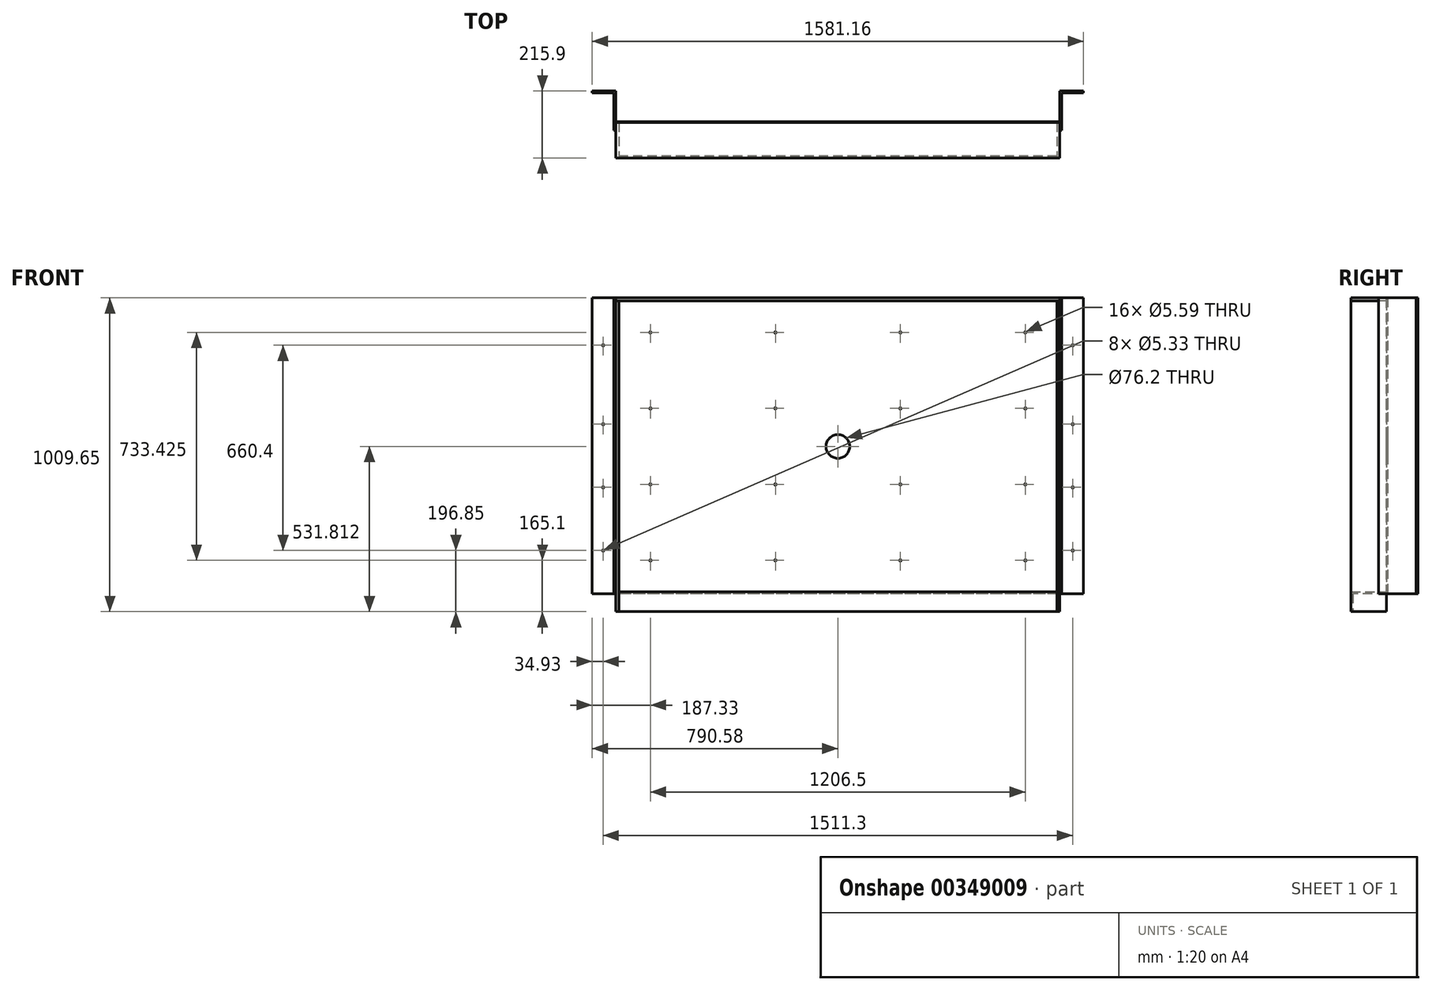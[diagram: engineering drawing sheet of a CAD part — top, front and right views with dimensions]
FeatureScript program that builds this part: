
annotation { "Feature Type Name" : "Feature", "Feature Type Description" : "" }
export const myFeature = defineFeature(function(context is Context, id is Id, definition is map)
    precondition{}
    {
        {
            assignVariable(context, id + "F0", {"name" : "OuterFrameWidth", "anyValue" : 1428.75 * mm});
        }
        {
            var Q0;
            Q0=qCreatedBy(makeId("Right.planeOp"),FACE);
            var sketch = newSketch(context, id + "F1", { "sketchPlane" : qUnion([Q0])});
            skLineSegment(sketch, "E0", {"start": v(0, 0) * mm, "end": v(-111.12, 0) * mm});
            skLineSegment(sketch, "E1", {"start": v(-111.12, 0) * mm, "end": v(-111.12, -57.15) * mm});
            skLineSegment(sketch, "E2", {"start": v(-111.12, -57.15) * mm, "end": v(-117.47, -57.15) * mm});
            skLineSegment(sketch, "E3", {"start": v(-117.47, -57.15) * mm, "end": v(-117.47, 6.35) * mm});
            skLineSegment(sketch, "E4", {"start": v(-117.48, 6.35) * mm, "end": v(-3.17, 6.35) * mm});
            skLineSegment(sketch, "E5", {"start": v(-3.18, 0) * mm, "end": v(-3.18, 952.5) * mm});
            skLineSegment(sketch, "E6", {"start": v(-3.18, 942.98) * mm, "end": v(-117.48, 942.98) * mm});
            skLineSegment(sketch, "E7", {"start": v(-117.48, 942.98) * mm, "end": v(-117.48, 952.5) * mm});
            skLineSegment(sketch, "E8", {"start": v(-117.48, 952.5) * mm, "end": v(0, 952.5) * mm});
            skLineSegment(sketch, "E9", {"start": v(0, 952.5) * mm, "end": v(0, 0) * mm});
            skLineSegment(sketch, "E10", {"start": v(98.42, 917.94) * mm, "end": v(98.42, 187.98) * mm, "construction": true});
            skSolve(sketch);
        }
        {
            var Q0;
            {var subQ7=sQuery(id+"F1.wireOp",EDGE,"E9");Q0=makeQuery(id+"F1.imprint","IMPRINT",FACE,{"disambiguationData":[TD([[makeQuery(id+"F1.imprint","IMPRINT",EDGE,{"derivedFrom":subQ7}),-1.0]])]});}
            extrude(context, id + "F2", {"entities" : qUnion([Q0]), "endBound" : BoundingType.SYMMETRIC, "depth" : getVariable(context, 'OuterFrameWidth')});
        }
        {
            var Q0;
            {var subQ3=sQuery(id+"F1.wireOp",EDGE,"E6");Q0=makeQuery(id+"F1.imprint","IMPRINT",FACE,{"disambiguationData":[TD([[makeQuery(id+"F1.imprint","IMPRINT",EDGE,{"derivedFrom":subQ3}),-1.0]])]});}
            extrude(context, id + "F3", {"entities" : qUnion([Q0]), "endBound" : BoundingType.SYMMETRIC, "depth" : getVariable(context, 'OuterFrameWidth')});
        }
        {
            var Q0;
            {var subQ0=sQuery(id+"F1.wireOp",EDGE,"E1");Q0=makeQuery(id+"F1.imprint","IMPRINT",FACE,{"disambiguationData":[TD([[makeQuery(id+"F1.imprint","IMPRINT",EDGE,{"derivedFrom":subQ0}),-1.0]])]});}
            extrude(context, id + "F4", {"entities" : qUnion([Q0]), "endBound" : BoundingType.SYMMETRIC, "depth" : getVariable(context, 'OuterFrameWidth') - 19.05 * mm});
        }
        {
            var Q0;
            Q0=makeQuery(id+"F3.opExtrude","CAP_FACE",FACE,{"disambiguationData":[OSD([sQuery(id+"F1.wireOp",EDGE,"E5"),sQuery(id+"F1.wireOp",EDGE,"E6"),sQuery(id+"F1.wireOp",EDGE,"E7"),sQuery(id+"F1.wireOp",EDGE,"E8")])],"isStart":true});
            var sketch = newSketch(context, id + "F5", { "sketchPlane" : qUnion([Q0])});
            skLineSegment(sketch, "E11.bottom", {"start": v(3.17, 942.98) * mm, "end": v(117.47, 942.98) * mm});
            skLineSegment(sketch, "E11.top", {"start": v(3.18, -57.15) * mm, "end": v(117.47, -57.15) * mm});
            skLineSegment(sketch, "E11.left", {"start": v(3.18, 942.98) * mm, "end": v(3.18, -57.15) * mm});
            skLineSegment(sketch, "E11.right", {"start": v(117.47, 942.98) * mm, "end": v(117.47, -57.15) * mm});
            skSolve(sketch);
        }
        {
            var Q0;
            Q0 = qSketchRegion(id + "F5", true);
            var Q1;
            Q1=makeQuery(id+"F4.opExtrude","CAP_FACE",FACE,{"disambiguationData":[OSD([sQuery(id+"F1.wireOp",EDGE,"E0"),sQuery(id+"F1.wireOp",EDGE,"E1"),sQuery(id+"F1.wireOp",EDGE,"E2"),sQuery(id+"F1.wireOp",EDGE,"E3"),sQuery(id+"F1.wireOp",EDGE,"E4"),sQuery(id+"F1.wireOp",EDGE,"E5")])],"isStart":true});
            extrude(context, id + "F6", {"entities" : qUnion([Q0]), "endBound" : BoundingType.UP_TO_SURFACE, "oppositeDirection" : true, "endBoundEntityFace" : qUnion([Q1]), "depth" : 25.4 * mm});
        }
        {
            var Q0;
            Q0=makeQuery(id+"F6.opExtrude","SWEPT_BODY",BODY,{"disambiguationData":[OSD([sQuery(id+"F5.wireOp",EDGE,"E11.bottom"),sQuery(id+"F5.wireOp",EDGE,"E11.top"),sQuery(id+"F5.wireOp",EDGE,"E11.left"),sQuery(id+"F5.wireOp",EDGE,"E11.right")])]});
            var Q1;
            Q1=qCreatedBy(makeId("Right.planeOp"),FACE);
            mirror(context, id + "F7", {"entities" : qUnion([Q0]), "mirrorPlane" : qUnion([Q1])});
        }
        {
            var Q0;
            Q0=makeQuery(id+"F2.opExtrude","SWEPT_FACE",FACE,{"disambiguationData":[OSD([sQuery(id+"F1.wireOp",EDGE,"E5")])]});
            var sketch = newSketch(context, id + "F8", { "sketchPlane" : qUnion([Q0])});
            skLineSegment(sketch, "E12.bottom", {"start": v(-603.25, 841.38) * mm, "end": v(603.25, 841.38) * mm, "construction": true});
            skLineSegment(sketch, "E12.top", {"start": v(-603.25, 107.95) * mm, "end": v(603.25, 107.95) * mm, "construction": true});
            skLineSegment(sketch, "E12.left", {"start": v(-603.25, 841.38) * mm, "end": v(-603.25, 107.95) * mm, "construction": true});
            skLineSegment(sketch, "E12.right", {"start": v(603.25, 841.38) * mm, "end": v(603.25, 107.95) * mm, "construction": true});
            skLineSegment(sketch, "E13", {"start": v(-603.25, 596.9) * mm, "end": v(603.25, 596.9) * mm, "construction": true});
            skLineSegment(sketch, "E14", {"start": v(-603.25, 352.43) * mm, "end": v(603.25, 352.43) * mm, "construction": true});
            skLineSegment(sketch, "E15", {"start": v(-201.08, 841.38) * mm, "end": v(-201.08, 107.95) * mm, "construction": true});
            skLineSegment(sketch, "E16", {"start": v(201.08, 841.38) * mm, "end": v(201.08, 107.95) * mm, "construction": true});
            skLineSegment(sketch, "E17", {"start": v(0, 0) * mm, "end": v(0, 841.38) * mm, "construction": true});
            skLineSegment(sketch, "E18", {"start": v(-771.98, 474.66) * mm, "end": v(821.12, 474.66) * mm, "construction": true});
            skCircle(sketch, "E19", {"center": v(-603.25, 841.38) * mm, "radius": 2.8 * mm});
            skCircle(sketch, "E20", {"center": v(-201.08, 841.38) * mm, "radius": 2.8 * mm});
            skCircle(sketch, "E21", {"center": v(201.08, 841.38) * mm, "radius": 2.8 * mm});
            skCircle(sketch, "E22", {"center": v(603.25, 841.38) * mm, "radius": 2.8 * mm});
            skCircle(sketch, "E23", {"center": v(603.25, 596.9) * mm, "radius": 2.8 * mm});
            skCircle(sketch, "E24", {"center": v(603.25, 352.43) * mm, "radius": 2.8 * mm});
            skCircle(sketch, "E25", {"center": v(603.25, 107.95) * mm, "radius": 2.8 * mm});
            skCircle(sketch, "E26", {"center": v(201.08, 107.95) * mm, "radius": 2.8 * mm});
            skCircle(sketch, "E27", {"center": v(201.08, 596.9) * mm, "radius": 2.8 * mm});
            skCircle(sketch, "E28", {"center": v(201.08, 352.43) * mm, "radius": 2.8 * mm});
            skCircle(sketch, "E29", {"center": v(-201.08, 352.43) * mm, "radius": 2.8 * mm});
            skCircle(sketch, "E30", {"center": v(-201.08, 596.9) * mm, "radius": 2.8 * mm});
            skCircle(sketch, "E31", {"center": v(-201.08, 107.95) * mm, "radius": 2.8 * mm});
            skCircle(sketch, "E32", {"center": v(-603.25, 107.95) * mm, "radius": 2.8 * mm});
            skCircle(sketch, "E33", {"center": v(-603.25, 596.9) * mm, "radius": 2.8 * mm});
            skCircle(sketch, "E34", {"center": v(-603.25, 352.43) * mm, "radius": 2.8 * mm});
            skCircle(sketch, "E35", {"center": v(0, 474.66) * mm, "radius": 38.1 * mm});
            skLineSegment(sketch, "E36.bottom", {"start": v(-679.45, 917.58) * mm, "end": v(679.45, 917.58) * mm, "construction": true});
            skLineSegment(sketch, "E36.top", {"start": v(-679.45, 31.75) * mm, "end": v(679.45, 31.75) * mm, "construction": true});
            skLineSegment(sketch, "E36.left", {"start": v(-679.45, 917.58) * mm, "end": v(-679.45, 31.75) * mm, "construction": true});
            skLineSegment(sketch, "E36.right", {"start": v(679.45, 917.58) * mm, "end": v(679.45, 31.75) * mm, "construction": true});
            skLineSegment(sketch, "E37.bottom", {"start": v(-704.85, 942.98) * mm, "end": v(704.85, 942.98) * mm, "construction": true});
            skLineSegment(sketch, "E37.top", {"start": v(-704.85, 6.35) * mm, "end": v(704.85, 6.35) * mm, "construction": true});
            skLineSegment(sketch, "E37.left", {"start": v(-704.85, 942.98) * mm, "end": v(-704.85, 6.35) * mm, "construction": true});
            skLineSegment(sketch, "E37.right", {"start": v(704.85, 942.98) * mm, "end": v(704.85, 6.35) * mm, "construction": true});
            skLineSegment(sketch, "E38.top", {"start": v(-679.45, 133.35) * mm, "end": v(679.45, 133.35) * mm, "construction": true});
            skLineSegment(sketch, "E38.left", {"start": v(-679.45, 31.75) * mm, "end": v(-679.45, 133.35) * mm, "construction": true});
            skLineSegment(sketch, "E38.right", {"start": v(679.45, 31.75) * mm, "end": v(679.45, 133.35) * mm, "construction": true});
            skSolve(sketch);
        }
        {
            var Q0;
            Q0 = qSketchRegion(id + "F8", true);
            extrude(context, id + "F9", {"entities" : qUnion([Q0]), "operationType" : NewBodyOperationType.REMOVE, "endBound" : BoundingType.THROUGH_ALL, "oppositeDirection" : true, "depth" : 25.4 * mm});
        }
        {
            var Q0;
            Q0=qCreatedBy(makeId("Top.planeOp"),FACE);
            var sketch = newSketch(context, id + "F10", { "sketchPlane" : qUnion([Q0])});
            skLineSegment(sketch, "E39", {"start": v(-790.58, 98.42) * mm, "end": v(-714.38, 98.42) * mm});
            skLineSegment(sketch, "E40", {"start": v(-714.38, 98.42) * mm, "end": v(-714.38, -28.58) * mm});
            skLineSegment(sketch, "E41", {"start": v(-714.38, -28.58) * mm, "end": v(-720.73, -28.58) * mm});
            skLineSegment(sketch, "E42", {"start": v(-720.73, -28.58) * mm, "end": v(-720.73, 92.07) * mm});
            skLineSegment(sketch, "E43", {"start": v(-720.73, 92.07) * mm, "end": v(-790.58, 92.07) * mm});
            skLineSegment(sketch, "E44", {"start": v(-790.58, 98.42) * mm, "end": v(-790.58, 92.07) * mm});
            skSolve(sketch);
        }
        {
            var Q0;
            Q0 = qSketchRegion(id + "F10", true);
            var Q1;
            Q1=makeQuery(id+"F3.opExtrude","SWEPT_FACE",FACE,{"disambiguationData":[OSD([sQuery(id+"F1.wireOp",EDGE,"E8")])]});
            extrude(context, id + "F11", {"entities" : qUnion([Q0]), "endBound" : BoundingType.UP_TO_SURFACE, "endBoundEntityFace" : qUnion([Q1]), "depth" : 25.4 * mm});
        }
        {
            var Q0;
            Q0=makeQuery(id+"F11.opExtrude","SWEPT_FACE",FACE,{"disambiguationData":[OSD([sQuery(id+"F10.wireOp",EDGE,"E43")])]});
            var sketch = newSketch(context, id + "F12", { "sketchPlane" : qUnion([Q0])});
            skCircle(sketch, "E45", {"center": v(-755.65, 800.1) * mm, "radius": 2.67 * mm});
            skCircle(sketch, "E46", {"center": v(-755.65, 546.1) * mm, "radius": 2.67 * mm});
            skCircle(sketch, "E47", {"center": v(-755.65, 139.7) * mm, "radius": 2.67 * mm});
            skLineSegment(sketch, "E48", {"start": v(-755.65, 800.1) * mm, "end": v(-755.65, 139.7) * mm, "construction": true});
            skPoint(sketch, "E49", {"position": v(-755.65, 952.5) * mm});
            skCircle(sketch, "E50", {"center": v(-755.65, 342.9) * mm, "radius": 2.67 * mm});
            skSolve(sketch);
        }
        {
            var Q0;
            Q0 = qSketchRegion(id + "F12", true);
            extrude(context, id + "F13", {"entities" : qUnion([Q0]), "operationType" : NewBodyOperationType.REMOVE, "endBound" : BoundingType.THROUGH_ALL, "oppositeDirection" : true, "depth" : 25.4 * mm});
        }
        {
            var Q0;
            Q0=makeQuery(id+"F11.opExtrude","SWEPT_BODY",BODY,{"disambiguationData":[OSD([sQuery(id+"F10.wireOp",EDGE,"E39"),sQuery(id+"F10.wireOp",EDGE,"E40"),sQuery(id+"F10.wireOp",EDGE,"E41"),sQuery(id+"F10.wireOp",EDGE,"E42"),sQuery(id+"F10.wireOp",EDGE,"E43"),sQuery(id+"F10.wireOp",EDGE,"E44")])]});
            var Q1;
            Q1=qCreatedBy(makeId("Right.planeOp"),FACE);
            mirror(context, id + "F14", {"entities" : qUnion([Q0]), "mirrorPlane" : qUnion([Q1])});
        }
    });
